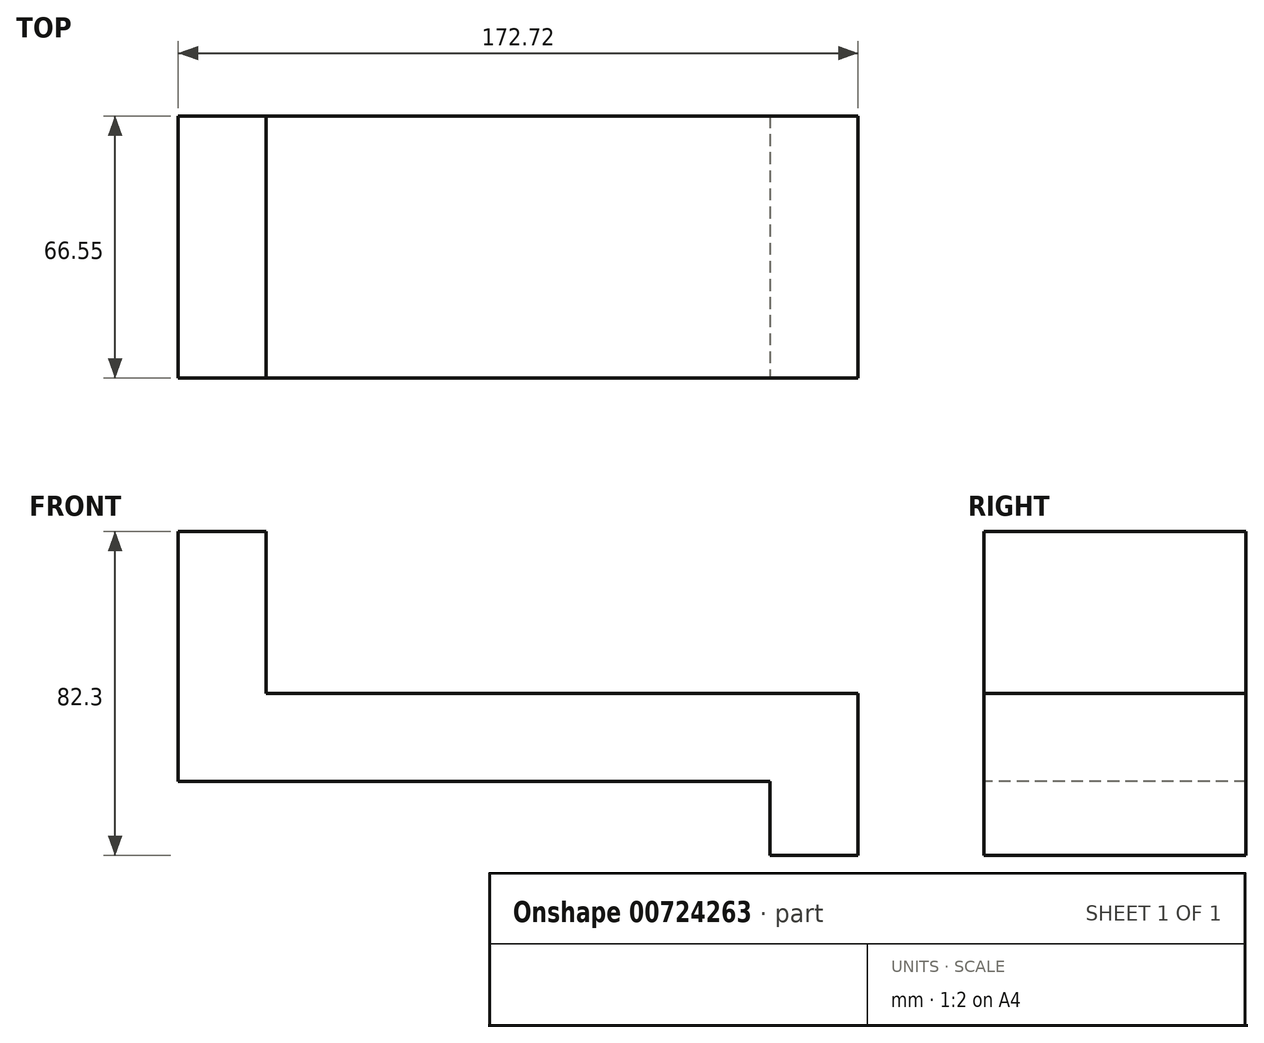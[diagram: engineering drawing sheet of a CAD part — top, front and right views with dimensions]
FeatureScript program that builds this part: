
annotation { "Feature Type Name" : "Feature", "Feature Type Description" : "" }
export const myFeature = defineFeature(function(context is Context, id is Id, definition is map)
    precondition{}
    {
        {
            var Q0;
            Q0=qCreatedBy(makeId("Front.planeOp"),FACE);
            var sketch = newSketch(context, id + "F0", { "sketchPlane" : qUnion([Q0])});
            skLineSegment(sketch, "E0", {"start": v(-75.7, 69.9) * mm, "end": v(-75.7, 6.4) * mm});
            skLineSegment(sketch, "E1", {"start": v(-75.7, 6.4) * mm, "end": v(74.66, 6.4) * mm});
            skLineSegment(sketch, "E2", {"start": v(74.66, 6.4) * mm, "end": v(74.66, -12.4) * mm});
            skLineSegment(sketch, "E3", {"start": v(97.01, -12.4) * mm, "end": v(74.66, -12.4) * mm});
            skLineSegment(sketch, "E4", {"start": v(97.01, 28.75) * mm, "end": v(97.01, -12.4) * mm});
            skLineSegment(sketch, "E5", {"start": v(97.01, 28.75) * mm, "end": v(-53.36, 28.75) * mm});
            skLineSegment(sketch, "E6", {"start": v(-75.7, 69.9) * mm, "end": v(-53.36, 69.9) * mm});
            skLineSegment(sketch, "E7", {"start": v(-53.36, 69.9) * mm, "end": v(-53.36, 28.75) * mm});
            skSolve(sketch);
        }
        {
            var Q0;
            Q0=makeQuery(id+"F0.imprint","IMPRINT",FACE,{"disambiguationData":[TD([[makeQuery(id+"F0.imprint","IMPRINT",EDGE,{"derivedFrom":sQuery(id+"F0.wireOp",EDGE,"E0")}),1.0]])]});
            extrude(context, id + "F1", {"entities" : qUnion([Q0]), "oppositeDirection" : true, "depth" : 66.55 * mm, "offsetDistance" : 25.4 * mm});
        }
    });
